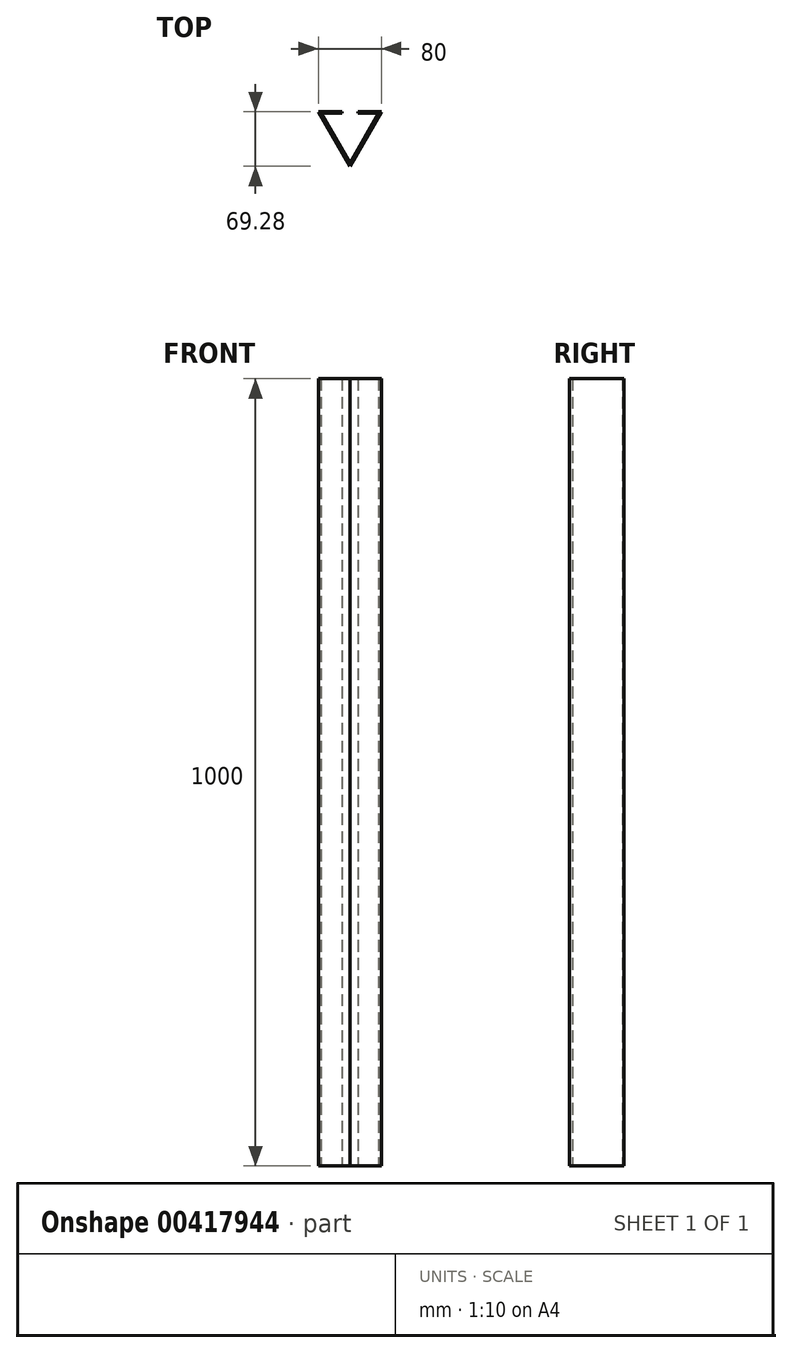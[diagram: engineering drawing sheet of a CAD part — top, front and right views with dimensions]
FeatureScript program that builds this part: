
annotation { "Feature Type Name" : "Feature", "Feature Type Description" : "" }
export const myFeature = defineFeature(function(context is Context, id is Id, definition is map)
    precondition{}
    {
        {
            var Q0;
            Q0=qCreatedBy(makeId("Top.planeOp"),FACE);
            var sketch = newSketch(context, id + "F0", { "sketchPlane" : qUnion([Q0])});
            skCircle(sketch, "E0.cCircle", {"center": v(0, 0) * mm, "radius": 46.19 * mm, "construction": true});
            skLineSegment(sketch, "E0.0", {"start": v(0, -46.19) * mm, "end": v(-40, 23.1) * mm});
            skLineSegment(sketch, "E0.1", {"start": v(-40, 23.1) * mm, "end": v(-10, 23.1) * mm});
            skLineSegment(sketch, "E0.2", {"start": v(40, 23.1) * mm, "end": v(0, -46.19) * mm});
            skLineSegment(sketch, "E1", {"start": v(10, 23.1) * mm, "end": v(40, 23.1) * mm});
            skLineSegment(sketch, "E2.0", {"start": v(-36.54, 21.1) * mm, "end": v(-10, 21.1) * mm});
            skLineSegment(sketch, "E2.1", {"start": v(0, -42.19) * mm, "end": v(-36.54, 21.1) * mm});
            skLineSegment(sketch, "E2.2", {"start": v(36.54, 21.1) * mm, "end": v(0, -42.19) * mm});
            skLineSegment(sketch, "E2.3", {"start": v(10, 21.1) * mm, "end": v(36.54, 21.1) * mm});
            skLineSegment(sketch, "E3", {"start": v(-10, 23.1) * mm, "end": v(-10, 21.1) * mm});
            skLineSegment(sketch, "E4", {"start": v(10, 23.1) * mm, "end": v(10, 21.1) * mm});
            skSolve(sketch);
        }
        {
            var Q0;
            Q0=makeQuery(id+"F0.imprint","IMPRINT",FACE,{"disambiguationData":[TD([[makeQuery(id+"F0.imprint","IMPRINT",EDGE,{"derivedFrom":sQuery(id+"F0.wireOp",EDGE,"E0.0")}),-1.0]])]});
            extrude(context, id + "F1", {"entities" : qUnion([Q0]), "depth" : 1000 * mm, "offsetDistance" : 25 * mm});
        }
    });
